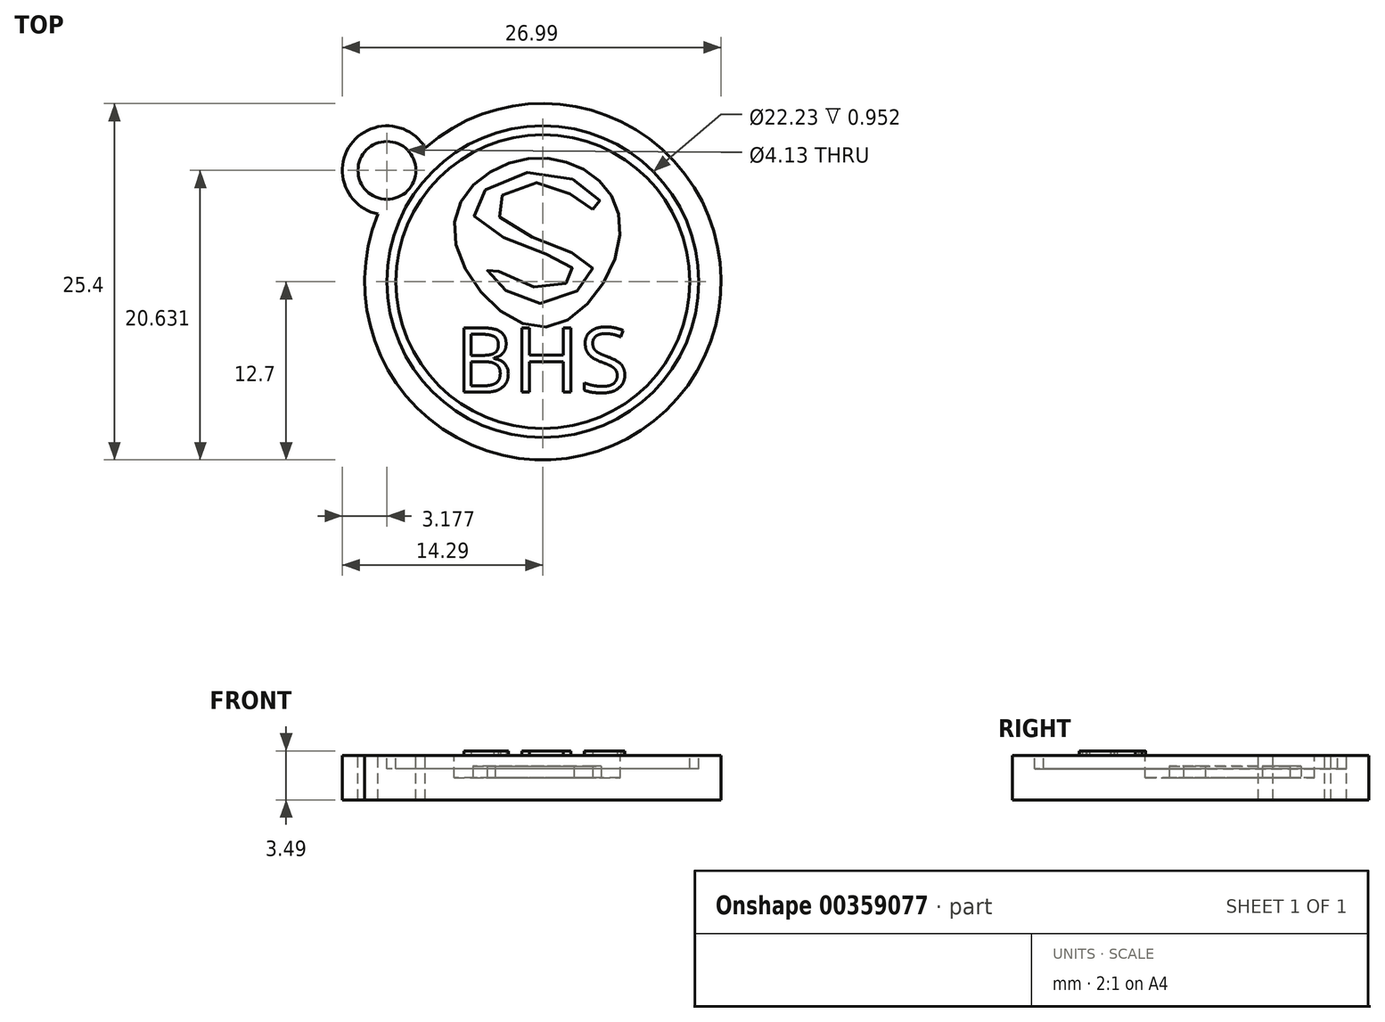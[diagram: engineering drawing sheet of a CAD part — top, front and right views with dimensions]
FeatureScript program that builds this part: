
annotation { "Feature Type Name" : "Feature", "Feature Type Description" : "" }
export const myFeature = defineFeature(function(context is Context, id is Id, definition is map)
    precondition{}
    {
        {
            var Q0;
            Q0=qCreatedBy(makeId("Top.planeOp"),FACE);
            var sketch = newSketch(context, id + "F0", { "sketchPlane" : qUnion([Q0])});
            skCircle(sketch, "E0", {"center": v(0, 0) * mm, "radius": 12.7 * mm});
            skSolve(sketch);
        }
        {
            var Q0;
            Q0=makeQuery(id+"F0.imprint","IMPRINT",FACE,{"disambiguationData":[TD([[makeQuery(id+"F0.imprint","IMPRINT",EDGE,{"derivedFrom":sQuery(id+"F0.wireOp",EDGE,"E0")}),1.0]])]});
            extrude(context, id + "F1", {"entities" : qUnion([Q0]), "depth" : 3.17 * mm});
        }
        {
            var Q0;
            Q0=makeQuery(id+"F1.opExtrude","CAP_FACE",FACE,{"disambiguationData":[OSD([sQuery(id+"F0.wireOp",EDGE,"E0")])],"isStart":false});
            var sketch = newSketch(context, id + "F2", { "sketchPlane" : qUnion([Q0])});
            skCircle(sketch, "E1", {"center": v(0, 0) * mm, "radius": 11.11 * mm});
            skCircle(sketch, "E2", {"center": v(0, 0) * mm, "radius": 10.48 * mm});
            skSolve(sketch);
        }
        {
            var Q0;
            Q0 = qSketchRegion(id + "F2", true);
            extrude(context, id + "F3", {"entities" : qUnion([Q0]), "operationType" : NewBodyOperationType.REMOVE, "oppositeDirection" : true, "depth" : 0.95 * mm});
        }
        {
            var Q0;
            Q0=makeQuery(id+"F1.opExtrude","CAP_FACE",FACE,{"disambiguationData":[OSD([sQuery(id+"F0.wireOp",EDGE,"E0")])],"isStart":false});
            var sketch = newSketch(context, id + "F4", { "sketchPlane" : qUnion([Q0])});
            skLineSegment(sketch, "E3", {"start": v(0, 0) * mm, "end": v(-11.11, 7.93) * mm, "construction": true});
            skLineSegment(sketch, "E4", {"start": v(-11.11, 7.93) * mm, "end": v(-11.11, 0) * mm, "construction": true});
            skLineSegment(sketch, "E5", {"start": v(-11.11, 0) * mm, "end": v(0, 0) * mm, "construction": true});
            skCircle(sketch, "E6", {"center": v(-11.11, 7.93) * mm, "radius": 3.18 * mm});
            skSolve(sketch);
        }
        {
            var Q0;
            {var subQ0=sQuery(id+"F4.wireOp",EDGE,"E6");var subQ1=makeQuery(id+"F1.opExtrude","CAP_EDGE",EDGE,{"disambiguationData":[OSD([sQuery(id+"F0.wireOp",EDGE,"E0")])],"isStart":false});var subQ2=makeQuery(id+"F4.imprint","INTERSECT",VERTEX,{"disambiguationData":[OD(0.0)],"derivedFrom":[subQ1,subQ0]});Q0=makeQuery(id+"F4.imprint","IMPRINT",FACE,{"disambiguationData":[TD([[makeQuery(id+"F4.imprint","IMPRINT",EDGE,{"disambiguationData":[TD([[subQ2,1.0]])],"derivedFrom":subQ0}),1.0]])]});}
            extrude(context, id + "F5", {"entities" : qUnion([Q0]), "operationType" : NewBodyOperationType.ADD, "oppositeDirection" : true, "depth" : 3.17 * mm});
        }
        {
            var Q0;
            {var subQ0=sQuery(id+"F4.wireOp",EDGE,"E6");var subQ1=makeQuery(id+"F1.opExtrude","CAP_EDGE",EDGE,{"disambiguationData":[OSD([sQuery(id+"F0.wireOp",EDGE,"E0")])],"isStart":false});var subQ2=makeQuery(id+"F4.imprint","INTERSECT",VERTEX,{"disambiguationData":[OD(0.0)],"derivedFrom":[subQ1,subQ0]});Q0=makeQuery(id+"F4.imprint","IMPRINT",FACE,{"disambiguationData":[TD([[makeQuery(id+"F4.imprint","IMPRINT",EDGE,{"disambiguationData":[TD([[subQ2,1.0]])],"derivedFrom":subQ0}),1.0]])]});}
            var sketch = newSketch(context, id + "F6", { "sketchPlane" : qUnion([Q0])});
            skCircle(sketch, "E7", {"center": v(-11.11, 7.93) * mm, "radius": 2.06 * mm});
            skLineSegment(sketch, "E8.0", {"start": v(0, 0) * mm, "end": v(-11.11, 7.93) * mm, "construction": true});
            skLineSegment(sketch, "E9.0", {"start": v(-11.11, 7.93) * mm, "end": v(-11.11, 0) * mm, "construction": true});
            skSolve(sketch);
        }
        {
            var Q0;
            {var subQ0=sQuery(id+"F6.wireOp",EDGE,"E7");var subQ1=sQuery(id+"F4.wireOp",EDGE,"E6");var subQ2=makeQuery(id+"F1.opExtrude","CAP_EDGE",EDGE,{"disambiguationData":[OSD([sQuery(id+"F0.wireOp",EDGE,"E0")])],"isStart":false});var subQ3=makeQuery(id+"F4.imprint","IMPRINT",EDGE,{"disambiguationData":[TD([[makeQuery(id+"F4.imprint","INTERSECT",VERTEX,{"disambiguationData":[OD(0.0)],"derivedFrom":[subQ2,subQ1]}),1.0]])],"derivedFrom":subQ2});var subQ4=makeQuery(id+"F6.imprint","INTERSECT",VERTEX,{"disambiguationData":[OD(0.0)],"derivedFrom":[subQ3,subQ0]});Q0=makeQuery(id+"F6.imprint","IMPRINT",FACE,{"disambiguationData":[TD([[makeQuery(id+"F6.imprint","IMPRINT",EDGE,{"disambiguationData":[TD([[subQ4,1.0]])],"derivedFrom":subQ0}),1.0]])]});}
            var Q1;
            {var subQ0=sQuery(id+"F6.wireOp",EDGE,"E7");var subQ1=sQuery(id+"F4.wireOp",EDGE,"E6");var subQ2=makeQuery(id+"F1.opExtrude","CAP_EDGE",EDGE,{"disambiguationData":[OSD([sQuery(id+"F0.wireOp",EDGE,"E0")])],"isStart":false});var subQ3=makeQuery(id+"F4.imprint","IMPRINT",EDGE,{"disambiguationData":[TD([[makeQuery(id+"F4.imprint","INTERSECT",VERTEX,{"disambiguationData":[OD(0.0)],"derivedFrom":[subQ2,subQ1]}),1.0]])],"derivedFrom":subQ2});var subQ4=makeQuery(id+"F6.imprint","INTERSECT",VERTEX,{"disambiguationData":[OD(0.0)],"derivedFrom":[subQ3,subQ0]});Q1=makeQuery(id+"F6.imprint","IMPRINT",FACE,{"disambiguationData":[TD([[makeQuery(id+"F6.imprint","IMPRINT",EDGE,{"disambiguationData":[TD([[subQ4,-1.0]])],"derivedFrom":subQ0}),1.0]])]});}
            var Q2;
            Q2=sQuery(id+"F6.wireOp",EDGE,"E7");
            extrude(context, id + "F7", {"entities" : qUnion([Q0, Q1]), "operationType" : NewBodyOperationType.REMOVE, "surfaceEntities" : qUnion([Q2]), "endBound" : BoundingType.UP_TO_NEXT, "oppositeDirection" : true, "depth" : 25.4 * mm});
        }
        {
            var Q0;
            Q0=makeQuery(id+"F2.imprint","IMPRINT",FACE,{"disambiguationData":[TD([[makeQuery(id+"F2.imprint","IMPRINT",EDGE,{"derivedFrom":sQuery(id+"F2.wireOp",EDGE,"E2")}),1.0]])]});
            var sketch = newSketch(context, id + "F8", { "sketchPlane" : qUnion([Q0])});
            skFitSpline(sketch, "E10", {"points": [v(3.56, 5.13) * mm, v(0.3, 7.02) * mm, v(-3.38, 5.4) * mm, v(0.44, 2.69) * mm, v(3.56, 0.81) * mm, v(0, -1.54) * mm, v(-3.78, 0.5) * mm, v(-3.92, 1.05) * mm, v(0, -0.5) * mm, v(2.22, 0.6) * mm, v(0, 2.05) * mm, v(-5, 5.07) * mm, v(0, 7.85) * mm, v(4.16, 5.44) * mm, v(3.56, 5.13) * mm]});
            skFitSpline(sketch, "E11", {"points": [v(5.5, 3.32) * mm, v(0, -3.24) * mm, v(-6.31, 3.4) * mm, v(-2.74, 8.32) * mm, v(2.82, 8.05) * mm, v(5.5, 3.32) * mm]});
            skSolve(sketch);
        }
        {
            var Q0;
            Q0=makeQuery(id+"F8.imprint","IMPRINT",FACE,{"disambiguationData":[TD([[makeQuery(id+"F8.imprint","IMPRINT",EDGE,{"derivedFrom":sQuery(id+"F8.wireOp",EDGE,"E10")}),-1.0]])]});
            var Q1;
            Q1=sQuery(id+"F8.wireOp",EDGE,"E10");
            extrude(context, id + "F9", {"entities" : qUnion([Q0]), "operationType" : NewBodyOperationType.REMOVE, "surfaceEntities" : qUnion([Q1]), "oppositeDirection" : true, "depth" : 0.76 * mm});
        }
        {
            var Q0;
            Q0=makeQuery(id+"F8.imprint","IMPRINT",FACE,{"disambiguationData":[TD([[makeQuery(id+"F8.imprint","IMPRINT",EDGE,{"derivedFrom":sQuery(id+"F8.wireOp",EDGE,"E10")}),1.0]])]});
            extrude(context, id + "F10", {"entities" : qUnion([Q0]), "operationType" : NewBodyOperationType.REMOVE, "oppositeDirection" : true, "depth" : 1.59 * mm});
        }
        {
            var Q0;
            Q0=makeQuery(id+"F2.imprint","IMPRINT",FACE,{"disambiguationData":[TD([[makeQuery(id+"F2.imprint","IMPRINT",EDGE,{"derivedFrom":sQuery(id+"F2.wireOp",EDGE,"E2")}),1.0]])]});
            var sketch = newSketch(context, id + "F11", { "sketchPlane" : qUnion([Q0])});
            skText(sketch, "E12", { "text": "BHS", "fontName": "OpenSans-Regular.ttf"});
            const initialGuessF11  = {"E12": [-0.00627, -0.00787, 1, 0, 0.00462]};
            skSetInitialGuess(sketch, initialGuessF11);
            skSolve(sketch);
        }
        {
            var Q0;
            Q0 = qSketchRegion(id + "F11", true);
            extrude(context, id + "F12", {"entities" : qUnion([Q0]), "operationType" : NewBodyOperationType.ADD, "depth" : 0.32 * mm});
        }
    });
